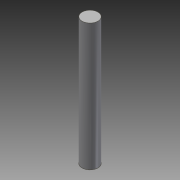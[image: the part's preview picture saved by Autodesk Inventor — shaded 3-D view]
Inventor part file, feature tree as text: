
AUTODESK INVENTOR PART (.ipt)
format: ipt  version: 2014 SP1 (Build 180222100, 222)  size: 69,632 bytes
history: native  units: in
note: dims shown in document units (in); Inventor stores cm internally (conversion verified against a paired STEP export)
features: extrude x1, sketch x1
ambient origin geometry x8: Origin, YZ Plane, XZ Plane, XY Plane, X Axis, Y Axis, Z Axis, Center Point
bodies: Solid1 (feature_tree)
feature tree (2):
  extrude  "Extrusion1"  Depth=3.0in TaperAngle=0.0deg
  sketch  "Sketch1"  dims[d0=0.375in d1=3.0in d2=0.0in]
